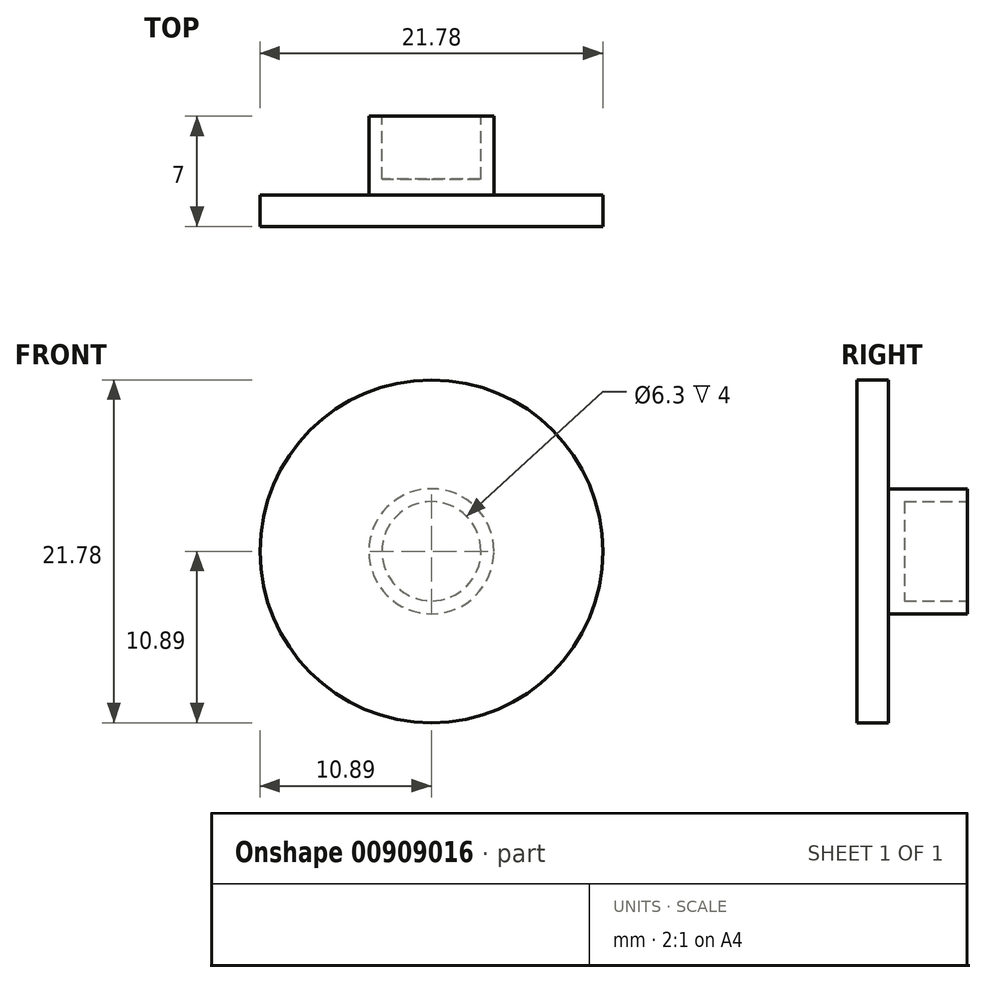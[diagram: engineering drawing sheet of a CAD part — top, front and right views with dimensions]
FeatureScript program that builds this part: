
annotation { "Feature Type Name" : "Feature", "Feature Type Description" : "" }
export const myFeature = defineFeature(function(context is Context, id is Id, definition is map)
    precondition{}
    {
        {
            var Q0;
            Q0=qCreatedBy(makeId("Front.planeOp"),FACE);
            var sketch = newSketch(context, id + "F0", { "sketchPlane" : qUnion([Q0])});
            skCircle(sketch, "E0", {"center": v(0, 0) * mm, "radius": 10.89 * mm});
            skSolve(sketch);
        }
        {
            var Q0;
            Q0=qSketchRegion(id+"F0",true);
            extrude(context, id + "F1", {"entities" : qUnion([Q0]), "depth" : 2 * mm, "offsetDistance" : 25 * mm});
        }
        {
            var Q0;
            Q0=makeQuery(id+"F1.opExtrude","CAP_FACE",FACE,{"disambiguationData":[OSD([sQuery(id+"F0.wireOp",EDGE,"E0")])],"isStart":true});
            var sketch = newSketch(context, id + "F2", { "sketchPlane" : qUnion([Q0])});
            skCircle(sketch, "E1", {"center": v(0, 0) * mm, "radius": 3.98 * mm});
            skSolve(sketch);
        }
        {
            var Q0;
            Q0=qSketchRegion(id+"F2",true);
            extrude(context, id + "F3", {"entities" : qUnion([Q0]), "operationType" : NewBodyOperationType.ADD, "depth" : 5 * mm, "offsetDistance" : 25 * mm});
        }
        {
            var Q0;
            Q0=makeQuery(id+"F3.opExtrude","CAP_FACE",FACE,{"disambiguationData":[OSD([sQuery(id+"F2.wireOp",EDGE,"E1")])],"isStart":false});
            var sketch = newSketch(context, id + "F4", { "sketchPlane" : qUnion([Q0])});
            skCircle(sketch, "E2", {"center": v(0, 0) * mm, "radius": 3.15 * mm});
            skSolve(sketch);
        }
        {
            var Q0;
            Q0=qSketchRegion(id+"F4",true);
            extrude(context, id + "F5", {"entities" : qUnion([Q0]), "operationType" : NewBodyOperationType.REMOVE, "oppositeDirection" : true, "depth" : 4 * mm, "offsetDistance" : 25 * mm});
        }
    });
